# Revit family: Casement_34_F_Side_Hung_Standard
name_source: partatom
category: Windows
revit_build: Autodesk Revit 2014 (Build: 20130308_1515(x64)
units: mm (PartAtom-declared; Revit-internal decimal feet)

## types (12) — shared parameters
Aluminium Thickness = 1 mm  [stored 0.00328084 ft]
Area Pane Left Top = 0.52 m²
Area Pane Right Top = 0.52 m²
Bead SG Gap = 13 mm  [stored 0.0426509 ft]
Casement Dimension = 34 mm  [stored 0.111549 ft]
Custom Sash Left Height = 1154 mm  [stored 3.78609 ft]
Custom Sash Left Width = 554 mm  [stored 1.81759 ft]
Custom Sash Right Height = 1154 mm  [stored 3.78609 ft]
Custom Sash Right Width = 554 mm  [stored 1.81759 ft]
DG Extrusion Start = 7 mm  [stored 0.0229659 ft]
DG Gasket Finish = Double Glazing Gasket Material
DG Thickness Calc = 4 mm  [stored 0.0131234 ft]
Default Sill Height = 800 mm  [stored 2.62467 ft]
Depth Bead = 20 mm  [stored 0.0656168 ft]
Description = Window 34mm, Type F side hung
Frame Center Offset = 17 mm
Height Sash Left = 1124 mm
Height Sash Left Opening = 1154 mm  [stored 3.78609 ft]
Height Sash Right = 1124 mm
Height Sash Right Opening = 1154 mm  [stored 3.78609 ft]
Length Transom Left = 540 mm  [stored 1.77165 ft]
Length Transom Right = 540 mm  [stored 1.77165 ft]
Limit Fixed Pane Height Max = 1800 mm  [stored 5.90551 ft]
Limit Fixed Pane Height Min = 200 mm  [stored 0.656168 ft]
Limit Fixed Pane Width Max = 1500 mm  [stored 4.92126 ft]
Limit Fixed Pane Width Min = 200 mm  [stored 0.656168 ft]
Limit Sash Height Max = 1500 mm  [stored 4.92126 ft]
Limit Sash Height Min = 300 mm  [stored 0.984252 ft]
Limit Sash Width Max = 700 mm  [stored 2.29659 ft]
Limit Sash Width Min = 300 mm  [stored 0.984252 ft]
Limit Window Height Max = 1860 mm
Limit Window Height Min = 1430 mm  [stored 4.6916 ft]
Limit Window Width Max = 2700 mm
Limit Window Width Min = 1400 mm
Manufacturer = Crealco
Max System DG One Piece Thickness = 4 mm  [stored 0.0131234 ft]
Max System DG Unit Thickness = 20 mm  [stored 0.0656168 ft]
Model = Casement 34
Offset Bead Center Reversed = 17 mm
Offset Fixed Panel Center Left = 600 mm  [stored 1.9685 ft]
Offset Mullion Left = 570 mm  [stored 1.87008 ft]
Offset Mullion Right = 570 mm  [stored 1.87008 ft]
Offset Sash Side = 23 mm  [stored 0.0754593 ft]
Offset Sash Top = 23 mm  [stored 0.0754593 ft]
Offset Transom Left Top = 1170 mm
Offset Transom Right Top = 1170 mm
Offset Window Exterior = 17 mm
SG Gasket Thickness = 6 mm  [stored 0.019685 ft]
Sash Center Offset = 14 mm  [stored 0.0459318 ft]
Sash Overlap = 7 mm  [stored 0.0229659 ft]
Sash Spacing Inner = 8 mm  [stored 0.0262467 ft]
Side Hung Left = Yes
Side Hung Right = No
URL = http://www.crealco.co.za
Wall Closure = By host
Width Bead = 15 mm  [stored 0.0492126 ft]
Width Fixed Panel Left = 540 mm  [stored 1.77165 ft]
Width Fixed Panel Right = 540 mm  [stored 1.77165 ft]
Width Profile = 30 mm  [stored 0.0984252 ft]
Width Sash Left = 524 mm  [stored 1.71916 ft]
Width Sash Left Opening = 554 mm  [stored 1.81759 ft]
Width Sash Right = 524 mm  [stored 1.71916 ft]
Width Sash Right Opening = 554 mm  [stored 1.81759 ft]
zero-valued in all types: Window Exterior Offset

## per-type parameters (varying)
- 34-1815SS-1000Pa: Area Pane Left Bottom=0.13 m²; Area Pane Middle=0.82 m²; Area Pane Right Bottom=0.13 m²; Clearvue Insulated LowE SHGC Value=0.552; Clearvue Insulated LowE U Value=3.73; Clearvue Insulated SHGC Value=0.625; Clearvue Insulated U Value=4.15; Clearvue SHGC Value=0.682; Clearvue U Value=6.65; Corrected Mullion Size=0 mm  [stored 0 ft]; Custom Windload=1000 mm  [stored 3.28084 ft]; Custom Window Height=1490 mm  [stored 4.88845 ft]; Custom Window Width=1790 mm  [stored 5.8727 ft]; Depth Mullion=54 mm  [stored 0.177165 ft]; Energy Advantage SHGC Value=0.612; Energy Advantage U Value=5.03; Height=1490 mm  [stored 4.88845 ft]; Height Fixed Panel Center=1430 mm  [stored 4.6916 ft]; Height Fixed Panel Left=260 mm; Height Fixed Panel Right=260 mm; Intruderprufe LowE SHGC Value=0.573; Intruderprufe SHGC Value=0.643; Intruderprufe U Value=6.32; Length Mullion=1490 mm  [stored 4.88845 ft]; Max Pane Area=0.82 m²; Mullion Depth Windload Based=54 mm  [stored 0.177165 ft]; Standard Mullion Different=0 mm  [stored 0 ft]; Width=1790 mm  [stored 5.8727 ft]; Width Fixed Panel Center=590 mm; Windload Design=1000 mm  [stored 3.28084 ft]
- 34-1815SS-1500Pa: Area Pane Left Bottom=0.13 m²; Area Pane Middle=0.82 m²; Area Pane Right Bottom=0.13 m²; Clearvue Insulated LowE SHGC Value=0.552; Clearvue Insulated LowE U Value=3.73; Clearvue Insulated SHGC Value=0.625; Clearvue Insulated U Value=4.15; Clearvue SHGC Value=6.85; Clearvue U Value=6.65; Corrected Mullion Size=0 mm  [stored 0 ft]; Custom Windload=1500 mm  [stored 4.92126 ft]; Custom Window Height=1490 mm  [stored 4.88845 ft]; Custom Window Width=1790 mm  [stored 5.8727 ft]; Depth Mullion=54 mm  [stored 0.177165 ft]; Energy Advantage SHGC Value=6.12; Energy Advantage U Value=5.03; Height=1490 mm  [stored 4.88845 ft]; Height Fixed Panel Center=1430 mm  [stored 4.6916 ft]; Height Fixed Panel Left=260 mm; Height Fixed Panel Right=260 mm; Intruderprufe LowE SHGC Value=0.573; Intruderprufe SHGC Value=0.643; Intruderprufe U Value=6.32; Length Mullion=1490 mm  [stored 4.88845 ft]; Max Pane Area=0.82 m²; Mullion Depth Windload Based=54 mm  [stored 0.177165 ft]; Standard Mullion Different=0 mm  [stored 0 ft]; Width=1790 mm  [stored 5.8727 ft]; Width Fixed Panel Center=590 mm; Windload Design=1500 mm  [stored 4.92126 ft]
- 34-1815SS-2000Pa: Area Pane Left Bottom=0.13 m²; Area Pane Middle=0.82 m²; Area Pane Right Bottom=0.13 m²; Clearvue Insulated LowE SHGC Value=0.552; Clearvue Insulated LowE U Value=3.73; Clearvue Insulated SHGC Value=0.625; Clearvue Insulated U Value=4.15; Clearvue SHGC Value=0.682; Clearvue U Value=6.65; Corrected Mullion Size=54 mm  [stored 0.177165 ft]; Custom Windload=2000 mm; Custom Window Height=1490 mm  [stored 4.88845 ft]; Custom Window Width=1790 mm  [stored 5.8727 ft]; Depth Mullion=54 mm  [stored 0.177165 ft]; Energy Advantage SHGC Value=0.612; Energy Advantage U Value=5.03; Height=1490 mm  [stored 4.88845 ft]; Height Fixed Panel Center=1430 mm  [stored 4.6916 ft]; Height Fixed Panel Left=260 mm; Height Fixed Panel Right=260 mm; Intruderprufe LowE SHGC Value=0.573; Intruderprufe SHGC Value=0.643; Intruderprufe U Value=6.32; Length Mullion=1490 mm  [stored 4.88845 ft]; Max Pane Area=0.82 m²; Mullion Depth Windload Based=54 mm  [stored 0.177165 ft]; Standard Mullion Different=1 mm  [stored 0.00328084 ft]; Width=1790 mm  [stored 5.8727 ft]; Width Fixed Panel Center=590 mm; Windload Design=2000 mm
- 34-2415SS-1000Pa: Area Pane Left Bottom=0.13 m²; Area Pane Middle=1.68 m²; Area Pane Right Bottom=0.13 m²; Clearvue Insulated LowE SHGC Value=0.608; Clearvue Insulated LowE U Value=3.52; Clearvue Insulated SHGC Value=0.682; Clearvue Insulated U Value=4.06; Clearvue SHGC Value=0; Clearvue U Value=7.9; Corrected Mullion Size=0 mm  [stored 0 ft]; Custom Windload=1000 mm  [stored 3.28084 ft]; Custom Window Height=1490 mm  [stored 4.88845 ft]; Custom Window Width=2390 mm; Depth Mullion=54 mm  [stored 0.177165 ft]; Energy Advantage SHGC Value=0; Energy Advantage U Value=7.9; Height=1490 mm  [stored 4.88845 ft]; Height Fixed Panel Center=1430 mm  [stored 4.6916 ft]; Height Fixed Panel Left=260 mm; Height Fixed Panel Right=260 mm; Intruderprufe LowE SHGC Value=0.631; Intruderprufe SHGC Value=0.71; Intruderprufe U Value=6.53; Length Mullion=1490 mm  [stored 4.88845 ft]; Max Pane Area=1.68 m²; Mullion Depth Windload Based=54 mm  [stored 0.177165 ft]; Standard Mullion Different=0 mm  [stored 0 ft]; Width=2390 mm; Width Fixed Panel Center=1190 mm  [stored 3.9042 ft]; Windload Design=1000 mm  [stored 3.28084 ft]
- 34-2415SS-1500Pa: Area Pane Left Bottom=0.13 m²; Area Pane Middle=1.68 m²; Area Pane Right Bottom=0.13 m²; Clearvue Insulated LowE SHGC Value=0.608; Clearvue Insulated LowE U Value=3.52; Clearvue Insulated SHGC Value=0.682; Clearvue Insulated U Value=4.06; Clearvue SHGC Value=0; Clearvue U Value=7.9; Corrected Mullion Size=0 mm  [stored 0 ft]; Custom Windload=1500 mm  [stored 4.92126 ft]; Custom Window Height=1490 mm  [stored 4.88845 ft]; Custom Window Width=2390 mm; Depth Mullion=54 mm  [stored 0.177165 ft]; Energy Advantage SHGC Value=0; Energy Advantage U Value=7.9; Height=1490 mm  [stored 4.88845 ft]; Height Fixed Panel Center=1430 mm  [stored 4.6916 ft]; Height Fixed Panel Left=260 mm; Height Fixed Panel Right=260 mm; Intruderprufe LowE SHGC Value=0.631; Intruderprufe SHGC Value=0.71; Intruderprufe U Value=6.53; Length Mullion=1490 mm  [stored 4.88845 ft]; Max Pane Area=1.68 m²; Mullion Depth Windload Based=54 mm  [stored 0.177165 ft]; Standard Mullion Different=0 mm  [stored 0 ft]; Width=2390 mm; Width Fixed Panel Center=1190 mm  [stored 3.9042 ft]; Windload Design=1500 mm  [stored 4.92126 ft]
- 34-2415SS-2000Pa: Area Pane Left Bottom=0.13 m²; Area Pane Middle=1.68 m²; Area Pane Right Bottom=0.13 m²; Clearvue Insulated LowE SHGC Value=0.61; Clearvue Insulated LowE U Value=3.57; Clearvue Insulated SHGC Value=0.67; Clearvue Insulated U Value=4.21; Clearvue SHGC Value=0; Clearvue U Value=7.9; Corrected Mullion Size=0 mm  [stored 0 ft]; Custom Windload=2000 mm; Custom Window Height=1490 mm  [stored 4.88845 ft]; Custom Window Width=2390 mm; Depth Mullion=70 mm  [stored 0.229659 ft]; Energy Advantage SHGC Value=0; Energy Advantage U Value=7.9; Height=1490 mm  [stored 4.88845 ft]; Height Fixed Panel Center=1430 mm  [stored 4.6916 ft]; Height Fixed Panel Left=260 mm; Height Fixed Panel Right=260 mm; Intruderprufe LowE SHGC Value=0.631; Intruderprufe SHGC Value=0.712; Intruderprufe U Value=6.74; Length Mullion=1490 mm  [stored 4.88845 ft]; Max Pane Area=1.68 m²; Mullion Depth Windload Based=70 mm  [stored 0.229659 ft]; Standard Mullion Different=0 mm  [stored 0 ft]; Width=2390 mm; Width Fixed Panel Center=1190 mm  [stored 3.9042 ft]; Windload Design=2000 mm
- 34-1818SS-1000Pa: Area Pane Left Bottom=0.29 m²; Area Pane Middle=1 m²; Area Pane Right Bottom=0.29 m²; Clearvue Insulated LowE SHGC Value=0.594; Clearvue Insulated LowE U Value=3.8; Clearvue Insulated SHGC Value=0.67; Clearvue Insulated U Value=4.27; Clearvue SHGC Value=0.734; Clearvue U Value=6.97; Corrected Mullion Size=0 mm  [stored 0 ft]; Custom Windload=1000 mm  [stored 3.28084 ft]; Custom Window Height=1790 mm  [stored 5.8727 ft]; Custom Window Width=1790 mm  [stored 5.8727 ft]; Depth Mullion=54 mm  [stored 0.177165 ft]; Energy Advantage SHGC Value=0.658; Energy Advantage U Value=5.21; Height=1790 mm  [stored 5.8727 ft]; Height Fixed Panel Center=1730 mm  [stored 5.67585 ft]; Height Fixed Panel Left=560 mm; Height Fixed Panel Right=560 mm; Intruderprufe LowE SHGC Value=0.616; Intruderprufe SHGC Value=0.692; Intruderprufe U Value=6.63; Length Mullion=1790 mm  [stored 5.8727 ft]; Max Pane Area=1 m²; Mullion Depth Windload Based=54 mm  [stored 0.177165 ft]; Standard Mullion Different=0 mm  [stored 0 ft]; Width=1790 mm  [stored 5.8727 ft]; Width Fixed Panel Center=590 mm; Windload Design=1000 mm  [stored 3.28084 ft]
- 34-1818SS-1500Pa: Area Pane Left Bottom=0.29 m²; Area Pane Middle=1 m²; Area Pane Right Bottom=0.29 m²; Clearvue Insulated LowE SHGC Value=0.596; Clearvue Insulated LowE U Value=3.86; Clearvue Insulated SHGC Value=0.655; Clearvue Insulated U Value=4.46; Clearvue SHGC Value=0.735; Clearvue U Value=7.05; Corrected Mullion Size=0 mm  [stored 0 ft]; Custom Windload=1500 mm  [stored 4.92126 ft]; Custom Window Height=1790 mm  [stored 5.8727 ft]; Custom Window Width=1790 mm  [stored 5.8727 ft]; Depth Mullion=70 mm  [stored 0.229659 ft]; Energy Advantage SHGC Value=0.658; Energy Advantage U Value=5.32; Height=1790 mm  [stored 5.8727 ft]; Height Fixed Panel Center=1730 mm  [stored 5.67585 ft]; Height Fixed Panel Left=560 mm; Height Fixed Panel Right=560 mm; Intruderprufe LowE SHGC Value=0.617; Intruderprufe SHGC Value=0.694; Intruderprufe U Value=6.9; Length Mullion=1790 mm  [stored 5.8727 ft]; Max Pane Area=1 m²; Mullion Depth Windload Based=70 mm  [stored 0.229659 ft]; Standard Mullion Different=0 mm  [stored 0 ft]; Width=1790 mm  [stored 5.8727 ft]; Width Fixed Panel Center=590 mm; Windload Design=1500 mm  [stored 4.92126 ft]
- 34-1818SS-2000Pa: Area Pane Left Bottom=0.29 m²; Area Pane Middle=1 m²; Area Pane Right Bottom=0.29 m²; Clearvue Insulated LowE SHGC Value=0.596; Clearvue Insulated LowE U Value=3.86; Clearvue Insulated SHGC Value=0.655; Clearvue Insulated U Value=4.46; Clearvue SHGC Value=0.735; Clearvue U Value=7.05; Corrected Mullion Size=0 mm  [stored 0 ft]; Custom Windload=2000 mm; Custom Window Height=1790 mm  [stored 5.8727 ft]; Custom Window Width=1790 mm  [stored 5.8727 ft]; Depth Mullion=70 mm  [stored 0.229659 ft]; Energy Advantage SHGC Value=0.658; Energy Advantage U Value=5.32; Height=1790 mm  [stored 5.8727 ft]; Height Fixed Panel Center=1730 mm  [stored 5.67585 ft]; Height Fixed Panel Left=560 mm; Height Fixed Panel Right=560 mm; Intruderprufe LowE SHGC Value=0.617; Intruderprufe SHGC Value=0.962; Intruderprufe U Value=6.9; Length Mullion=1790 mm  [stored 5.8727 ft]; Max Pane Area=1 m²; Mullion Depth Windload Based=70 mm  [stored 0.229659 ft]; Standard Mullion Different=0 mm  [stored 0 ft]; Width=1790 mm  [stored 5.8727 ft]; Width Fixed Panel Center=590 mm; Windload Design=2000 mm
- 34-2418SS-1000Pa: Area Pane Left Bottom=0.29 m²; Area Pane Middle=2.03 m²; Area Pane Right Bottom=0.29 m²; Clearvue Insulated LowE SHGC Value=0.672; Clearvue Insulated LowE U Value=3.75; Clearvue Insulated SHGC Value=0.738; Clearvue Insulated U Value=4.46; Clearvue SHGC Value=0; Clearvue U Value=7.9; Corrected Mullion Size=0 mm  [stored 0 ft]; Custom Windload=1000 mm  [stored 3.28084 ft]; Custom Window Height=1790 mm  [stored 5.8727 ft]; Custom Window Width=2390 mm; Depth Mullion=70 mm  [stored 0.229659 ft]; Energy Advantage SHGC Value=0; Energy Advantage U Value=7.9; Height=1790 mm  [stored 5.8727 ft]; Height Fixed Panel Center=1730 mm  [stored 5.67585 ft]; Height Fixed Panel Left=560 mm; Height Fixed Panel Right=560 mm; Intruderprufe LowE SHGC Value=0.695; Intruderprufe SHGC Value=0.785; Intruderprufe U Value=7.26; Length Mullion=1790 mm  [stored 5.8727 ft]; Max Pane Area=2.03 m²; Mullion Depth Windload Based=70 mm  [stored 0.229659 ft]; Standard Mullion Different=0 mm  [stored 0 ft]; Width=2390 mm; Width Fixed Panel Center=1190 mm  [stored 3.9042 ft]; Windload Design=1000 mm  [stored 3.28084 ft]
- 34-2418SS-1500Pa: Area Pane Left Bottom=0.29 m²; Area Pane Middle=2.03 m²; Area Pane Right Bottom=0.29 m²; Clearvue Insulated LowE SHGC Value=0.672; Clearvue Insulated LowE U Value=3.75; Clearvue Insulated SHGC Value=0.738; Clearvue Insulated U Value=4.46; Clearvue SHGC Value=0; Clearvue U Value=7.9; Corrected Mullion Size=0 mm  [stored 0 ft]; Custom Windload=1500 mm  [stored 4.92126 ft]; Custom Window Height=1790 mm  [stored 5.8727 ft]; Custom Window Width=2390 mm; Depth Mullion=70 mm  [stored 0.229659 ft]; Energy Advantage SHGC Value=0; Energy Advantage U Value=7.9; Height=1790 mm  [stored 5.8727 ft]; Height Fixed Panel Center=1730 mm  [stored 5.67585 ft]; Height Fixed Panel Left=560 mm; Height Fixed Panel Right=560 mm; Intruderprufe LowE SHGC Value=0.695; Intruderprufe SHGC Value=0.785; Intruderprufe U Value=7.26; Length Mullion=1790 mm  [stored 5.8727 ft]; Max Pane Area=2.03 m²; Mullion Depth Windload Based=70 mm  [stored 0.229659 ft]; Standard Mullion Different=0 mm  [stored 0 ft]; Width=2390 mm; Width Fixed Panel Center=1190 mm  [stored 3.9042 ft]; Windload Design=1500 mm  [stored 4.92126 ft]
- 34-2418SS-2000Pa: Area Pane Left Bottom=0.29 m²; Area Pane Middle=2.03 m²; Area Pane Right Bottom=0.29 m²; Clearvue Insulated LowE SHGC Value=0.672; Clearvue Insulated LowE U Value=3.75; Clearvue Insulated SHGC Value=0.738; Clearvue Insulated U Value=4.46; Clearvue SHGC Value=0; Clearvue U Value=7.9; Corrected Mullion Size=0 mm  [stored 0 ft]; Custom Windload=2000 mm; Custom Window Height=1790 mm  [stored 5.8727 ft]; Custom Window Width=2390 mm; Depth Mullion=70 mm  [stored 0.229659 ft]; Energy Advantage SHGC Value=0; Energy Advantage U Value=7.9; Height=1790 mm  [stored 5.8727 ft]; Height Fixed Panel Center=1730 mm  [stored 5.67585 ft]; Height Fixed Panel Left=560 mm; Height Fixed Panel Right=560 mm; Intruderprufe LowE SHGC Value=0.695; Intruderprufe SHGC Value=0.785; Intruderprufe U Value=7.26; Length Mullion=1790 mm  [stored 5.8727 ft]; Max Pane Area=2.03 m²; Mullion Depth Windload Based=70 mm  [stored 0.229659 ft]; Standard Mullion Different=0 mm  [stored 0 ft]; Width=2390 mm; Width Fixed Panel Center=1190 mm  [stored 3.9042 ft]; Windload Design=2000 mm

note: [stored X ft] marks values corroborated as IEEE doubles in the binary element streams (Revit-internal decimal feet)

## geometry (parser evidence)
native form markers: Extrusion x1, Sweep x29
no freeform markers — native parametric forms only
